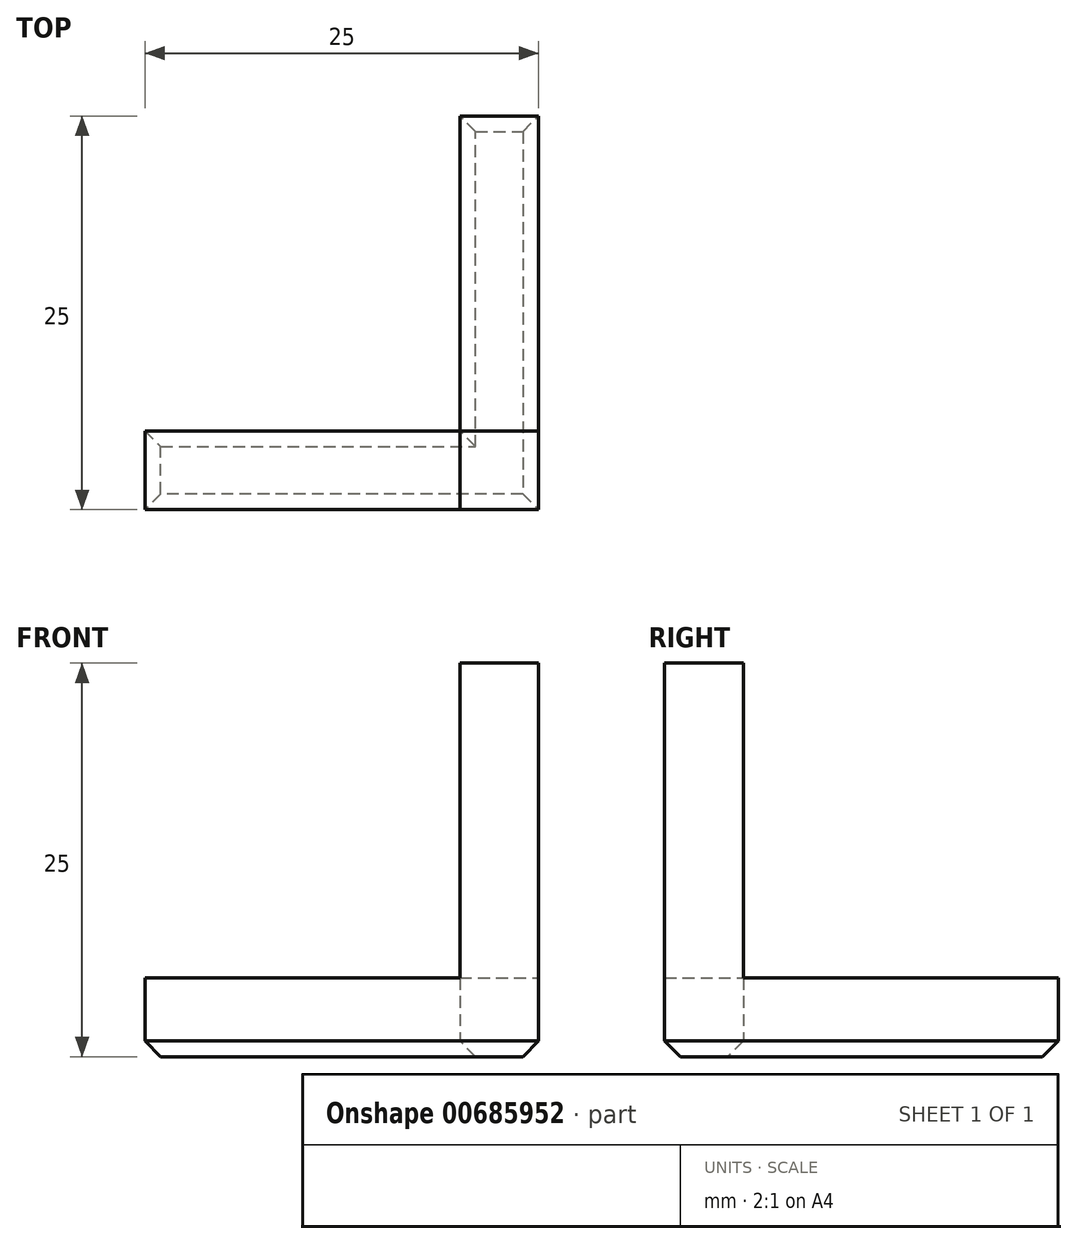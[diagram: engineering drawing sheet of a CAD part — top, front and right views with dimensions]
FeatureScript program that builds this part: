
annotation { "Feature Type Name" : "Feature", "Feature Type Description" : "" }
export const myFeature = defineFeature(function(context is Context, id is Id, definition is map)
    precondition{}
    {
        {
            var Q0;
            Q0=qCreatedBy(makeId("Top.planeOp"),FACE);
            var sketch = newSketch(context, id + "F0", { "sketchPlane" : qUnion([Q0])});
            skLineSegment(sketch, "E0", {"start": v(0, 0) * mm, "end": v(-25, 0) * mm});
            skLineSegment(sketch, "E1", {"start": v(-25, 0) * mm, "end": v(-25, 5) * mm});
            skLineSegment(sketch, "E2", {"start": v(-25, 5) * mm, "end": v(-5, 5) * mm});
            skLineSegment(sketch, "E3", {"start": v(-5, 5) * mm, "end": v(-5, 25) * mm});
            skLineSegment(sketch, "E4", {"start": v(-5, 25) * mm, "end": v(0, 25) * mm});
            skLineSegment(sketch, "E5", {"start": v(0, 25) * mm, "end": v(0, 0) * mm});
            skSolve(sketch);
        }
        {
            var Q0;
            Q0=makeQuery(id+"F0.imprint","IMPRINT",FACE,{"disambiguationData":[TD([[makeQuery(id+"F0.imprint","IMPRINT",EDGE,{"derivedFrom":sQuery(id+"F0.wireOp",EDGE,"E0")}),-1.0]])]});
            extrude(context, id + "F1", {"entities" : qUnion([Q0]), "depth" : 5 * mm, "offsetDistance" : 25 * mm});
        }
        {
            var Q0;
            Q0=makeQuery(id+"F1.opExtrude","CAP_FACE",FACE,{"disambiguationData":[OSD([sQuery(id+"F0.wireOp",EDGE,"E0"),sQuery(id+"F0.wireOp",EDGE,"E1"),sQuery(id+"F0.wireOp",EDGE,"E2"),sQuery(id+"F0.wireOp",EDGE,"E3"),sQuery(id+"F0.wireOp",EDGE,"E4"),sQuery(id+"F0.wireOp",EDGE,"E5")])],"isStart":false});
            var sketch = newSketch(context, id + "F2", { "sketchPlane" : qUnion([Q0])});
            skLineSegment(sketch, "E6.bottom", {"start": v(0, 0) * mm, "end": v(-5, 0) * mm});
            skLineSegment(sketch, "E6.top", {"start": v(0, 5) * mm, "end": v(-5, 5) * mm});
            skLineSegment(sketch, "E6.left", {"start": v(0, 0) * mm, "end": v(0, 5) * mm});
            skLineSegment(sketch, "E6.right", {"start": v(-5, 0) * mm, "end": v(-5, 5) * mm});
            skSolve(sketch);
        }
        {
            var Q0;
            Q0=makeQuery(id+"F2.imprint","IMPRINT",FACE,{"disambiguationData":[TD([[makeQuery(id+"F2.imprint","IMPRINT",EDGE,{"derivedFrom":sQuery(id+"F2.wireOp",EDGE,"E6.bottom")}),-1.0]])]});
            extrude(context, id + "F3", {"entities" : qUnion([Q0]), "operationType" : NewBodyOperationType.ADD, "depth" : 20 * mm, "offsetDistance" : 25 * mm});
        }
        {
            var Q0;
            Q0=makeQuery(id+"F1.opExtrude","CAP_FACE",FACE,{"disambiguationData":[OSD([sQuery(id+"F0.wireOp",EDGE,"E0"),sQuery(id+"F0.wireOp",EDGE,"E1"),sQuery(id+"F0.wireOp",EDGE,"E2"),sQuery(id+"F0.wireOp",EDGE,"E3"),sQuery(id+"F0.wireOp",EDGE,"E4"),sQuery(id+"F0.wireOp",EDGE,"E5")])],"isStart":true});
            chamfer(context, id + "F4", {"entities" : qUnion([Q0]), "width" : 1 * mm, "tangentPropagation" : true});
        }
    });
